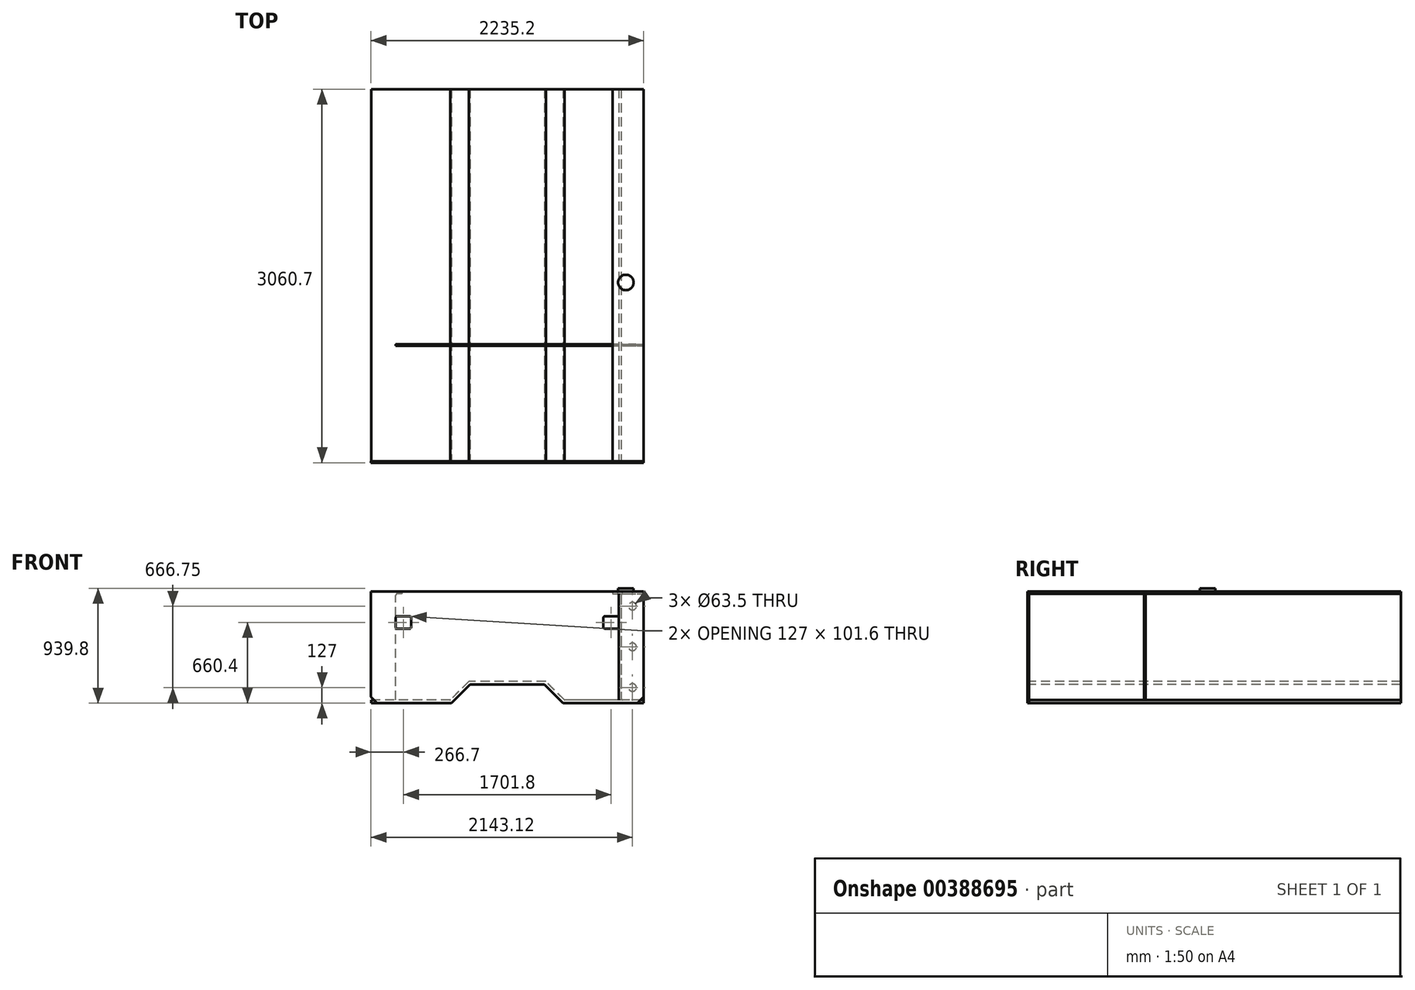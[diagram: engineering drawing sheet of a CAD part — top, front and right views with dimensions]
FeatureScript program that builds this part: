
annotation { "Feature Type Name" : "Feature", "Feature Type Description" : "" }
export const myFeature = defineFeature(function(context is Context, id is Id, definition is map)
    precondition{}
    {
        {
            var Q0;
            Q0=qCreatedBy(makeId("Front.planeOp"),FACE);
            var sketch = newSketch(context, id + "F0", { "sketchPlane" : qUnion([Q0])});
            skLineSegment(sketch, "E0", {"start": v(0, 0) * mm, "end": v(2235.2, 0) * mm});
            skLineSegment(sketch, "E1", {"start": v(2235.2, 0) * mm, "end": v(2235.2, -863.6) * mm});
            skLineSegment(sketch, "E2", {"start": v(2235.2, -863.6) * mm, "end": v(2184.4, -914.4) * mm});
            skLineSegment(sketch, "E3", {"start": v(2184.4, -914.4) * mm, "end": v(1574.8, -914.4) * mm});
            skLineSegment(sketch, "E4", {"start": v(1574.8, -914.4) * mm, "end": v(1422.4, -762) * mm});
            skLineSegment(sketch, "E5", {"start": v(1422.4, -762) * mm, "end": v(812.8, -762) * mm});
            skLineSegment(sketch, "E6", {"start": v(812.8, -762) * mm, "end": v(660.4, -914.4) * mm});
            skLineSegment(sketch, "E7", {"start": v(660.4, -914.4) * mm, "end": v(50.8, -914.4) * mm});
            skLineSegment(sketch, "E8", {"start": v(50.8, -914.4) * mm, "end": v(0, -863.6) * mm});
            skLineSegment(sketch, "E9", {"start": v(0, -863.6) * mm, "end": v(0, 0) * mm});
            skLineSegment(sketch, "E10", {"start": v(1117.6, 0) * mm, "end": v(1117.6, -2845.97) * mm, "construction": true});
            skPoint(sketch, "E11", {"position": v(1117.6, -762) * mm});
            skLineSegment(sketch, "E12.bottom", {"start": v(215.9, -203.2) * mm, "end": v(317.5, -203.2) * mm});
            skLineSegment(sketch, "E12.top", {"start": v(215.9, -304.8) * mm, "end": v(317.5, -304.8) * mm});
            skLineSegment(sketch, "E12.left", {"start": v(203.2, -215.9) * mm, "end": v(203.2, -292.1) * mm});
            skLineSegment(sketch, "E12.right", {"start": v(330.2, -215.9) * mm, "end": v(330.2, -292.1) * mm});
            skPoint(sketch, "E13.visualSharp", {"position": v(203.2, -203.2) * mm});
            skArc(sketch, "E13.filletArc", {"start": v(215.9, -203.2) * mm, "mid": v(206.92, -206.92) * mm, "end": v(203.2, -215.9) * mm});
            skPoint(sketch, "E14.visualSharp", {"position": v(330.2, -203.2) * mm});
            skArc(sketch, "E14.filletArc", {"start": v(330.2, -215.9) * mm, "mid": v(326.48, -206.92) * mm, "end": v(317.5, -203.2) * mm});
            skPoint(sketch, "E15.visualSharp", {"position": v(330.2, -304.8) * mm});
            skArc(sketch, "E15.filletArc", {"start": v(317.5, -304.8) * mm, "mid": v(326.48, -301.08) * mm, "end": v(330.2, -292.1) * mm});
            skPoint(sketch, "E16.visualSharp", {"position": v(203.2, -304.8) * mm});
            skArc(sketch, "E16.filletArc", {"start": v(203.2, -292.1) * mm, "mid": v(206.92, -301.08) * mm, "end": v(215.9, -304.8) * mm});
            skLineSegment(sketch, "E17.MirrorCS", {"start": v(1905, -215.9) * mm, "end": v(1905, -292.1) * mm});
            skPoint(sketch, "E18.MirrorP", {"position": v(1905, -304.8) * mm});
            skLineSegment(sketch, "E19.MirrorCS", {"start": v(2019.3, -304.8) * mm, "end": v(1917.7, -304.8) * mm});
            skLineSegment(sketch, "E20.MirrorCS", {"start": v(2032, -215.9) * mm, "end": v(2032, -292.1) * mm});
            skLineSegment(sketch, "E21.MirrorCS", {"start": v(2019.3, -203.2) * mm, "end": v(1917.7, -203.2) * mm});
            skArc(sketch, "E22.MirrorCS", {"start": v(1905, -215.9) * mm, "mid": v(1908.72, -206.92) * mm, "end": v(1917.7, -203.2) * mm});
            skArc(sketch, "E23.MirrorCS", {"start": v(1917.7, -304.8) * mm, "mid": v(1908.72, -301.08) * mm, "end": v(1905, -292.1) * mm});
            skArc(sketch, "E24.MirrorCS", {"start": v(2032, -292.1) * mm, "mid": v(2028.28, -301.08) * mm, "end": v(2019.3, -304.8) * mm});
            skArc(sketch, "E25.MirrorCS", {"start": v(2019.3, -203.2) * mm, "mid": v(2028.28, -206.92) * mm, "end": v(2032, -215.9) * mm});
            skSolve(sketch);
        }
        {
            var Q0;
            Q0 = qSketchRegion(id + "F0", true);
            extrude(context, id + "F1", {"entities" : qUnion([Q0]), "endBound" : BoundingType.SYMMETRIC, "depth" : 12.7 * mm});
        }
        {
            var Q0;
            Q0=makeQuery(id+"F1.opExtrude","CAP_FACE",FACE,{"disambiguationData":[OSD([sQuery(id+"F0.wireOp",EDGE,"E0"),sQuery(id+"F0.wireOp",EDGE,"E1"),sQuery(id+"F0.wireOp",EDGE,"E2"),sQuery(id+"F0.wireOp",EDGE,"E3"),sQuery(id+"F0.wireOp",EDGE,"E4"),sQuery(id+"F0.wireOp",EDGE,"E5"),sQuery(id+"F0.wireOp",EDGE,"E6"),sQuery(id+"F0.wireOp",EDGE,"E7"),sQuery(id+"F0.wireOp",EDGE,"E8"),sQuery(id+"F0.wireOp",EDGE,"E9"),sQuery(id+"F0.wireOp",EDGE,"E12.bottom"),sQuery(id+"F0.wireOp",EDGE,"E12.top"),sQuery(id+"F0.wireOp",EDGE,"E12.left"),sQuery(id+"F0.wireOp",EDGE,"E12.right"),sQuery(id+"F0.wireOp",EDGE,"E13.filletArc"),sQuery(id+"F0.wireOp",EDGE,"E14.filletArc"),sQuery(id+"F0.wireOp",EDGE,"E15.filletArc"),sQuery(id+"F0.wireOp",EDGE,"E16.filletArc"),sQuery(id+"F0.wireOp",EDGE,"E17.MirrorCS"),sQuery(id+"F0.wireOp",EDGE,"E19.MirrorCS"),sQuery(id+"F0.wireOp",EDGE,"E20.MirrorCS"),sQuery(id+"F0.wireOp",EDGE,"E21.MirrorCS"),sQuery(id+"F0.wireOp",EDGE,"E22.MirrorCS"),sQuery(id+"F0.wireOp",EDGE,"E23.MirrorCS"),sQuery(id+"F0.wireOp",EDGE,"E24.MirrorCS"),sQuery(id+"F0.wireOp",EDGE,"E25.MirrorCS")])],"isStart":true});
            var sketch = newSketch(context, id + "F2", { "sketchPlane" : qUnion([Q0])});
            skLineSegment(sketch, "E26", {"start": v(-2235.2, 0) * mm, "end": v(-1981.2, 0) * mm});
            skLineSegment(sketch, "E27", {"start": v(-1981.2, 0) * mm, "end": v(-1981.2, -19.05) * mm});
            skLineSegment(sketch, "E28", {"start": v(-1981.2, -19.05) * mm, "end": v(-2235.2, -19.05) * mm});
            skLineSegment(sketch, "E29", {"start": v(-2235.2, -19.05) * mm, "end": v(-2235.2, 0) * mm});
            skSolve(sketch);
        }
        {
            var Q0;
            Q0 = qSketchRegion(id + "F2", true);
            extrude(context, id + "F3", {"entities" : qUnion([Q0]), "depth" : 3048 * mm});
        }
        {
            var Q0;
            Q0=makeQuery(id+"F1.opExtrude","CAP_FACE",FACE,{"disambiguationData":[OSD([sQuery(id+"F0.wireOp",EDGE,"E0"),sQuery(id+"F0.wireOp",EDGE,"E1"),sQuery(id+"F0.wireOp",EDGE,"E2"),sQuery(id+"F0.wireOp",EDGE,"E3"),sQuery(id+"F0.wireOp",EDGE,"E4"),sQuery(id+"F0.wireOp",EDGE,"E5"),sQuery(id+"F0.wireOp",EDGE,"E6"),sQuery(id+"F0.wireOp",EDGE,"E7"),sQuery(id+"F0.wireOp",EDGE,"E8"),sQuery(id+"F0.wireOp",EDGE,"E9"),sQuery(id+"F0.wireOp",EDGE,"E12.bottom"),sQuery(id+"F0.wireOp",EDGE,"E12.top"),sQuery(id+"F0.wireOp",EDGE,"E12.left"),sQuery(id+"F0.wireOp",EDGE,"E12.right"),sQuery(id+"F0.wireOp",EDGE,"E13.filletArc"),sQuery(id+"F0.wireOp",EDGE,"E14.filletArc"),sQuery(id+"F0.wireOp",EDGE,"E15.filletArc"),sQuery(id+"F0.wireOp",EDGE,"E16.filletArc"),sQuery(id+"F0.wireOp",EDGE,"E17.MirrorCS"),sQuery(id+"F0.wireOp",EDGE,"E19.MirrorCS"),sQuery(id+"F0.wireOp",EDGE,"E20.MirrorCS"),sQuery(id+"F0.wireOp",EDGE,"E21.MirrorCS"),sQuery(id+"F0.wireOp",EDGE,"E22.MirrorCS"),sQuery(id+"F0.wireOp",EDGE,"E23.MirrorCS"),sQuery(id+"F0.wireOp",EDGE,"E24.MirrorCS"),sQuery(id+"F0.wireOp",EDGE,"E25.MirrorCS")])],"isStart":true});
            var sketch = newSketch(context, id + "F4", { "sketchPlane" : qUnion([Q0])});
            skLineSegment(sketch, "E30", {"start": v(-2235.2, -914.4) * mm, "end": v(-1574.8, -914.4) * mm});
            skLineSegment(sketch, "E31.0", {"start": v(-1422.4, -762) * mm, "end": v(-812.8, -762) * mm});
            skLineSegment(sketch, "E31.1", {"start": v(-1574.8, -914.4) * mm, "end": v(-1422.4, -762) * mm});
            skLineSegment(sketch, "E31.2", {"start": v(-812.8, -762) * mm, "end": v(-660.4, -914.4) * mm});
            skLineSegment(sketch, "E32.0", {"start": v(-660.4, -914.4) * mm, "end": v(-1.43, -914.4) * mm});
            skPoint(sketch, "E33.orphan", {"position": v(-50.8, -914.4) * mm});
            skLineSegment(sketch, "E34.0", {"start": v(-649.88, -889) * mm, "end": v(-1.43, -889) * mm});
            skLineSegment(sketch, "E34.1", {"start": v(-2235.2, -889) * mm, "end": v(-1585.32, -889) * mm});
            skLineSegment(sketch, "E34.2", {"start": v(-1585.32, -889) * mm, "end": v(-1432.92, -736.6) * mm});
            skLineSegment(sketch, "E34.3", {"start": v(-1432.92, -736.6) * mm, "end": v(-802.28, -736.6) * mm});
            skLineSegment(sketch, "E34.4", {"start": v(-802.28, -736.6) * mm, "end": v(-649.88, -889) * mm});
            skLineSegment(sketch, "E35", {"start": v(-2235.2, -889) * mm, "end": v(-2235.2, -914.4) * mm});
            skLineSegment(sketch, "E36", {"start": v(-1.43, -889) * mm, "end": v(-1.43, -914.4) * mm});
            skSolve(sketch);
        }
        {
            var Q0;
            Q0 = qSketchRegion(id + "F4", true);
            extrude(context, id + "F5", {"entities" : qUnion([Q0]), "depth" : 3048 * mm});
        }
        {
            var Q0;
            Q0=makeQuery(id+"F1.opExtrude","CAP_FACE",FACE,{"disambiguationData":[OSD([sQuery(id+"F0.wireOp",EDGE,"E0"),sQuery(id+"F0.wireOp",EDGE,"E1"),sQuery(id+"F0.wireOp",EDGE,"E2"),sQuery(id+"F0.wireOp",EDGE,"E3"),sQuery(id+"F0.wireOp",EDGE,"E4"),sQuery(id+"F0.wireOp",EDGE,"E5"),sQuery(id+"F0.wireOp",EDGE,"E6"),sQuery(id+"F0.wireOp",EDGE,"E7"),sQuery(id+"F0.wireOp",EDGE,"E8"),sQuery(id+"F0.wireOp",EDGE,"E9"),sQuery(id+"F0.wireOp",EDGE,"E12.bottom"),sQuery(id+"F0.wireOp",EDGE,"E12.top"),sQuery(id+"F0.wireOp",EDGE,"E12.left"),sQuery(id+"F0.wireOp",EDGE,"E12.right"),sQuery(id+"F0.wireOp",EDGE,"E13.filletArc"),sQuery(id+"F0.wireOp",EDGE,"E14.filletArc"),sQuery(id+"F0.wireOp",EDGE,"E15.filletArc"),sQuery(id+"F0.wireOp",EDGE,"E16.filletArc"),sQuery(id+"F0.wireOp",EDGE,"E17.MirrorCS"),sQuery(id+"F0.wireOp",EDGE,"E19.MirrorCS"),sQuery(id+"F0.wireOp",EDGE,"E20.MirrorCS"),sQuery(id+"F0.wireOp",EDGE,"E21.MirrorCS"),sQuery(id+"F0.wireOp",EDGE,"E22.MirrorCS"),sQuery(id+"F0.wireOp",EDGE,"E23.MirrorCS"),sQuery(id+"F0.wireOp",EDGE,"E24.MirrorCS"),sQuery(id+"F0.wireOp",EDGE,"E25.MirrorCS")])],"isStart":true});
            var sketch = newSketch(context, id + "F6", { "sketchPlane" : qUnion([Q0])});
            skLineSegment(sketch, "E37", {"start": v(-2032, -889) * mm, "end": v(-2032, -19.03) * mm});
            skPoint(sketch, "E37.startSnap0", {"position": v(-2032, -254) * mm});
            skLineSegment(sketch, "E38.0", {"start": v(-2032, -19.05) * mm, "end": v(-2051.05, -19.05) * mm});
            skLineSegment(sketch, "E39", {"start": v(-2051.05, -19.05) * mm, "end": v(-2051.05, -889) * mm});
            skPoint(sketch, "E40.orphan", {"position": v(-2235.2, -19.05) * mm});
            skPoint(sketch, "E41.orphan", {"position": v(-1981.2, -19.05) * mm});
            skLineSegment(sketch, "E42.0", {"start": v(-2051.05, -889) * mm, "end": v(-2032, -889) * mm});
            skPoint(sketch, "E43.orphan", {"position": v(-2235.2, -889) * mm});
            skPoint(sketch, "E44.orphan", {"position": v(-1585.32, -889) * mm});
            skPoint(sketch, "E45.orphan", {"position": v(-2032, -914.4) * mm});
            skSolve(sketch);
        }
        {
            var Q0;
            Q0 = qSketchRegion(id + "F6", true);
            extrude(context, id + "F7", {"entities" : qUnion([Q0]), "depth" : 3048 * mm});
        }
        {
            var Q0;
            Q0=makeQuery(id+"F1.opExtrude","CAP_FACE",FACE,{"disambiguationData":[OSD([sQuery(id+"F0.wireOp",EDGE,"E0"),sQuery(id+"F0.wireOp",EDGE,"E1"),sQuery(id+"F0.wireOp",EDGE,"E2"),sQuery(id+"F0.wireOp",EDGE,"E3"),sQuery(id+"F0.wireOp",EDGE,"E4"),sQuery(id+"F0.wireOp",EDGE,"E5"),sQuery(id+"F0.wireOp",EDGE,"E6"),sQuery(id+"F0.wireOp",EDGE,"E7"),sQuery(id+"F0.wireOp",EDGE,"E8"),sQuery(id+"F0.wireOp",EDGE,"E9"),sQuery(id+"F0.wireOp",EDGE,"E12.bottom"),sQuery(id+"F0.wireOp",EDGE,"E12.top"),sQuery(id+"F0.wireOp",EDGE,"E12.left"),sQuery(id+"F0.wireOp",EDGE,"E12.right"),sQuery(id+"F0.wireOp",EDGE,"E13.filletArc"),sQuery(id+"F0.wireOp",EDGE,"E14.filletArc"),sQuery(id+"F0.wireOp",EDGE,"E15.filletArc"),sQuery(id+"F0.wireOp",EDGE,"E16.filletArc"),sQuery(id+"F0.wireOp",EDGE,"E17.MirrorCS"),sQuery(id+"F0.wireOp",EDGE,"E19.MirrorCS"),sQuery(id+"F0.wireOp",EDGE,"E20.MirrorCS"),sQuery(id+"F0.wireOp",EDGE,"E21.MirrorCS"),sQuery(id+"F0.wireOp",EDGE,"E22.MirrorCS"),sQuery(id+"F0.wireOp",EDGE,"E23.MirrorCS"),sQuery(id+"F0.wireOp",EDGE,"E24.MirrorCS"),sQuery(id+"F0.wireOp",EDGE,"E25.MirrorCS")])],"isStart":true});
            cPlane(context, id + "F8", {"entities" : qUnion([Q0]), "cplaneType" : CPlaneType.OFFSET, "offset" : 944.57 * mm, "width" : 152.4 * mm, "height" : 152.4 * mm});
        }
        {
            var Q0;
            Q0=qCreatedBy(id+"F8.planeOp",FACE);
            var sketch = newSketch(context, id + "F9", { "sketchPlane" : qUnion([Q0])});
            skLineSegment(sketch, "E46.0", {"start": v(-2032, -889) * mm, "end": v(-1587.95, -889) * mm});
            skLineSegment(sketch, "E47.0", {"start": v(-1432.92, -736.6) * mm, "end": v(-802.28, -736.6) * mm});
            skLineSegment(sketch, "E48.0", {"start": v(-647.25, -889) * mm, "end": v(-203.2, -889) * mm});
            skLineSegment(sketch, "E49.0", {"start": v(-802.28, -736.6) * mm, "end": v(-651.74, -887.14) * mm});
            skLineSegment(sketch, "E50.0", {"start": v(-1583.46, -887.14) * mm, "end": v(-1432.92, -736.6) * mm});
            skLineSegment(sketch, "E51.0", {"start": v(-2032, -889) * mm, "end": v(-2032, -304.8) * mm});
            skLineSegment(sketch, "E52.0", {"start": v(-1981.2, -19.05) * mm, "end": v(-2019.3, -19.05) * mm});
            skLineSegment(sketch, "E53.0", {"start": v(-1981.2, 0) * mm, "end": v(-1981.2, -19.05) * mm});
            skLineSegment(sketch, "E54.0", {"start": v(-2032, -203.2) * mm, "end": v(-1917.7, -203.2) * mm});
            skPoint(sketch, "E55.0", {"position": v(-1917.7, -203.2) * mm});
            skLineSegment(sketch, "E56.0", {"start": v(-1905, -215.9) * mm, "end": v(-1905, -292.1) * mm});
            skLineSegment(sketch, "E57.0", {"start": v(-2032, -304.8) * mm, "end": v(-1917.7, -304.8) * mm});
            skPoint(sketch, "E58.0", {"position": v(-1917.7, -304.8) * mm});
            skArc(sketch, "E59.0", {"start": v(-1917.7, -304.8) * mm, "mid": v(-1908.72, -301.08) * mm, "end": v(-1905, -292.1) * mm});
            skArc(sketch, "E60.0", {"start": v(-1905, -215.9) * mm, "mid": v(-1908.72, -206.92) * mm, "end": v(-1917.7, -203.2) * mm});
            skLineSegment(sketch, "E61.0", {"start": v(-1117.6, 0) * mm, "end": v(-1117.6, -2845.97) * mm, "construction": true});
            skPoint(sketch, "E62.orphan", {"position": v(-2235.2, -889) * mm});
            skPoint(sketch, "E63.orphan", {"position": v(-2235.2, -19.05) * mm});
            skPoint(sketch, "E64.orphan", {"position": v(-2019.3, -203.2) * mm});
            skPoint(sketch, "E65.orphan", {"position": v(-2019.3, -304.8) * mm});
            skLineSegment(sketch, "E66.trimOffspring", {"start": v(-2032, -203.2) * mm, "end": v(-2032, -31.75) * mm});
            skLineSegment(sketch, "E67.MirrorCS", {"start": v(-203.2, -889) * mm, "end": v(-203.2, -304.8) * mm});
            skLineSegment(sketch, "E68.MirrorCS", {"start": v(-203.2, -203.2) * mm, "end": v(-203.2, -31.75) * mm});
            skLineSegment(sketch, "E69.MirrorCS", {"start": v(-203.2, -304.8) * mm, "end": v(-317.5, -304.8) * mm});
            skLineSegment(sketch, "E70.MirrorCS", {"start": v(-203.2, -203.2) * mm, "end": v(-317.5, -203.2) * mm});
            skLineSegment(sketch, "E71.MirrorCS", {"start": v(-330.2, -215.9) * mm, "end": v(-330.2, -292.1) * mm});
            skLineSegment(sketch, "E72.MirrorCS", {"start": v(-254, -19.05) * mm, "end": v(-215.9, -19.05) * mm});
            skLineSegment(sketch, "E73.MirrorCS", {"start": v(-254, 0) * mm, "end": v(-254, -19.05) * mm});
            skArc(sketch, "E74.MirrorCS", {"start": v(-317.5, -304.8) * mm, "mid": v(-326.48, -301.08) * mm, "end": v(-330.2, -292.1) * mm});
            skArc(sketch, "E75.MirrorCS", {"start": v(-330.2, -215.9) * mm, "mid": v(-326.48, -206.92) * mm, "end": v(-317.5, -203.2) * mm});
            skPoint(sketch, "E76.orphan", {"position": v(-1.43, -889) * mm});
            skLineSegment(sketch, "E77", {"start": v(-1981.2, 0) * mm, "end": v(-254, 0) * mm});
            skPoint(sketch, "E78.visualSharp", {"position": v(-2032, -19.05) * mm});
            skArc(sketch, "E78.filletArc", {"start": v(-2019.3, -19.05) * mm, "mid": v(-2028.28, -22.77) * mm, "end": v(-2032, -31.75) * mm});
            skPoint(sketch, "E79.visualSharp", {"position": v(-203.2, -19.05) * mm});
            skArc(sketch, "E79.filletArc", {"start": v(-203.2, -31.75) * mm, "mid": v(-206.92, -22.77) * mm, "end": v(-215.9, -19.05) * mm});
            skPoint(sketch, "E80.visualSharp", {"position": v(-1585.32, -889) * mm});
            skArc(sketch, "E80.filletArc", {"start": v(-1587.95, -889) * mm, "mid": v(-1585.52, -888.52) * mm, "end": v(-1583.46, -887.14) * mm});
            skPoint(sketch, "E81.visualSharp", {"position": v(-649.88, -889) * mm});
            skArc(sketch, "E81.filletArc", {"start": v(-651.74, -887.14) * mm, "mid": v(-649.68, -888.52) * mm, "end": v(-647.25, -889) * mm});
            skSolve(sketch);
        }
        {
            var Q0;
            Q0 = qSketchRegion(id + "F9", true);
            extrude(context, id + "F10", {"entities" : qUnion([Q0]), "depth" : 12.7 * mm});
        }
        {
            var Q0;
            Q0=qCreatedBy(id+"F8.planeOp",FACE);
            var sketch = newSketch(context, id + "F11", { "sketchPlane" : qUnion([Q0])});
            skLineSegment(sketch, "E82.0", {"start": v(-2051.05, -31.75) * mm, "end": v(-2051.05, -876.3) * mm});
            skLineSegment(sketch, "E83.0", {"start": v(-2235.2, -889) * mm, "end": v(-2063.75, -889) * mm});
            skLineSegment(sketch, "E84.0", {"start": v(-2235.2, -19.05) * mm, "end": v(-2235.2, -889) * mm});
            skLineSegment(sketch, "E85.0", {"start": v(-2063.75, -19.05) * mm, "end": v(-2235.2, -19.05) * mm});
            skPoint(sketch, "E86.orphan", {"position": v(-2235.2, -863.6) * mm});
            skPoint(sketch, "E87.orphan", {"position": v(-2235.2, 0) * mm});
            skLineSegment(sketch, "E88", {"start": v(-2235.2, -454.02) * mm, "end": v(-2051.05, -454.02) * mm, "construction": true});
            skPoint(sketch, "E89.orphan", {"position": v(-1981.2, -19.05) * mm});
            skLineSegment(sketch, "E90", {"start": v(-2143.12, -19.05) * mm, "end": v(-2143.12, -889.01) * mm, "construction": true});
            skCircle(sketch, "E91", {"center": v(-2143.12, -120.65) * mm, "radius": 31.75 * mm});
            skCircle(sketch, "E92.MirrorC", {"center": v(-2143.12, -787.4) * mm, "radius": 31.75 * mm});
            skPoint(sketch, "E93.visualSharp", {"position": v(-2051.05, -19.05) * mm});
            skArc(sketch, "E93.filletArc", {"start": v(-2051.05, -31.75) * mm, "mid": v(-2054.77, -22.77) * mm, "end": v(-2063.75, -19.05) * mm});
            skPoint(sketch, "E94.orphan", {"position": v(-1585.32, -889) * mm});
            skPoint(sketch, "E95.visualSharp", {"position": v(-2051.05, -889) * mm});
            skArc(sketch, "E95.filletArc", {"start": v(-2063.75, -889) * mm, "mid": v(-2054.77, -885.28) * mm, "end": v(-2051.05, -876.3) * mm});
            skCircle(sketch, "E96", {"center": v(-2143.12, -454.03) * mm, "radius": 31.75 * mm});
            skSolve(sketch);
        }
        {
            var Q0;
            Q0 = qSketchRegion(id + "F11", true);
            extrude(context, id + "F12", {"entities" : qUnion([Q0]), "depth" : 12.7 * mm});
        }
        {
            var Q0;
            Q0=makeQuery(id+"F3.opExtrude","SWEPT_FACE",FACE,{"disambiguationData":[OSD([sQuery(id+"F2.wireOp",EDGE,"E26")])]});
            var sketch = newSketch(context, id + "F13", { "sketchPlane" : qUnion([Q0])});
            skCircle(sketch, "E97", {"center": v(2088.97, 1470.97) * mm, "radius": 63.5 * mm});
            skSolve(sketch);
        }
        {
            var Q0;
            Q0 = qSketchRegion(id + "F13", true);
            extrude(context, id + "F14", {"entities" : qUnion([Q0]), "depth" : 25.4 * mm});
        }
    });
